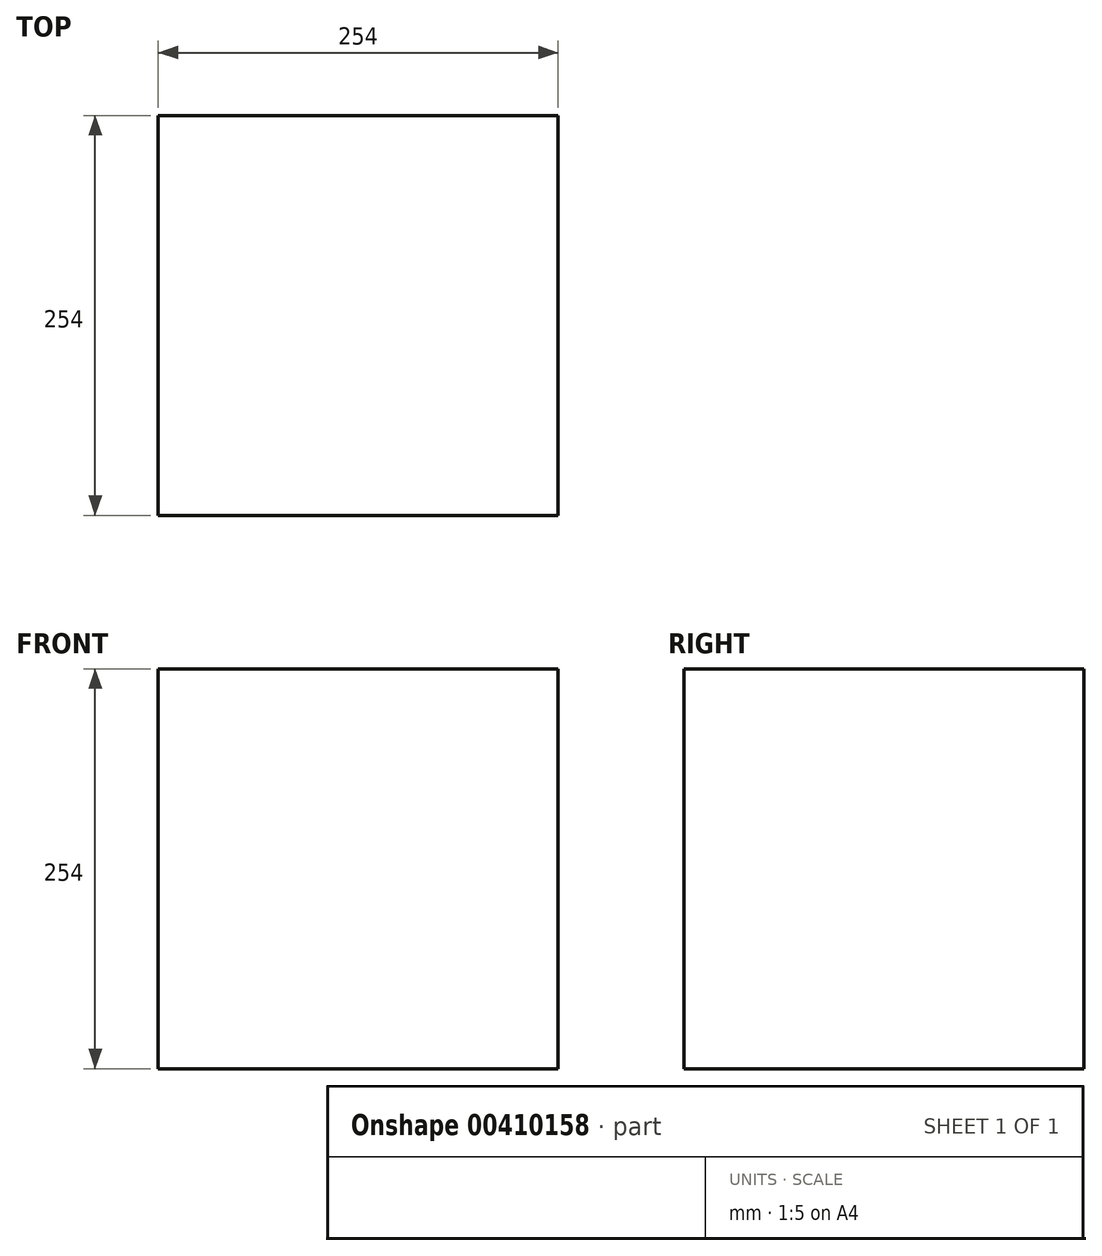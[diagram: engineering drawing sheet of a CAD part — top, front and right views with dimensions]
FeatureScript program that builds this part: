
annotation { "Feature Type Name" : "Feature", "Feature Type Description" : "" }
export const myFeature = defineFeature(function(context is Context, id is Id, definition is map)
    precondition{}
    {
        {
            var Q0;
            Q0=qCreatedBy(makeId("Top.planeOp"),FACE);
            var sketch = newSketch(context, id + "F0", { "sketchPlane" : qUnion([Q0])});
            skLineSegment(sketch, "E0.bottom", {"start": v(-127, -127) * mm, "end": v(127, -127) * mm});
            skLineSegment(sketch, "E0.top", {"start": v(-127, 127) * mm, "end": v(127, 127) * mm});
            skLineSegment(sketch, "E0.left", {"start": v(-127, -127) * mm, "end": v(-127, 127) * mm});
            skLineSegment(sketch, "E0.right", {"start": v(127, -127) * mm, "end": v(127, 127) * mm});
            skPoint(sketch, "E0.middle", {"position": v(0, 0) * mm});
            skSolve(sketch);
        }
        {
            var Q0;
            Q0 = qSketchRegion(id + "F0", true);
            extrude(context, id + "F1", {"entities" : qUnion([Q0]), "depth" : 254 * mm});
        }
        {
            var Q0;
            Q0=qCreatedBy(makeId("Top.planeOp"),FACE);
            cPlane(context, id + "F2", {"entities" : qUnion([Q0]), "cplaneType" : CPlaneType.OFFSET, "offset" : 127 * mm, "width" : 152.4 * mm, "height" : 152.4 * mm});
        }
    });
